FCSTD DOCUMENT  (FreeCAD 0.19R)
Label: key_dimensions
License: Creative Commons Attribution-ShareAlike
LicenseURL: http://creativecommons.org/licenses/by-sa/4.0/
objects: Spreadsheet::Sheet×1

FEATURE [Spreadsheet::Sheet] Spreadsheet  label="Dimensions"
  cells = A1=MDF thickness; A2(MDF_thick)=9; B2=MDF thick; A3(MDF_thin)=5.5; B3=MDF thin; A4=Main Frame; A5(frame_depth)=176; B5=Frame depth; A6(frame_width)=100; B6=Frame width; A7(window_width)=690; B7=Window width; A8(center_height)=299.25; B8=Center height (base to center); A9(cradle_base)=235; B9=Cradle base (base to cradle base); A10(slider_axis_height)=190; B10=slider axis height (base to horizontal sliders axis); A11(top_height)=1150; B11=Top height (top height, without curve top); A12(rear_overhang)=400; B12=Rear overhang (from the center); A13=Acrylic; A14(acrylic_width)=330; B14=width; A15(acrylic_depth)=469; B15=depth; A16=Cradle; A17(cradle_tilting)=40; B17=cradle tilting; A18(cradle_rounded)=15; B18=cradle rounded; A19(base_cradle_width)=400; B19=Base Cradle width; A20(base_cradle_depth)=320; B20=Base Cradle depth; A21=Base Rails; A22(rail_A)=38.5; B22=Rail A; A23(rail_B)=65.5; B23=Rail B; A24(rail_C)=115.5; B24=Rail C; A25(rail_D)=140.5; B25=Rail D; A26(wing_depth)=320; B26=Wing depth; A27(wing_length)=215; B27=Wing length
